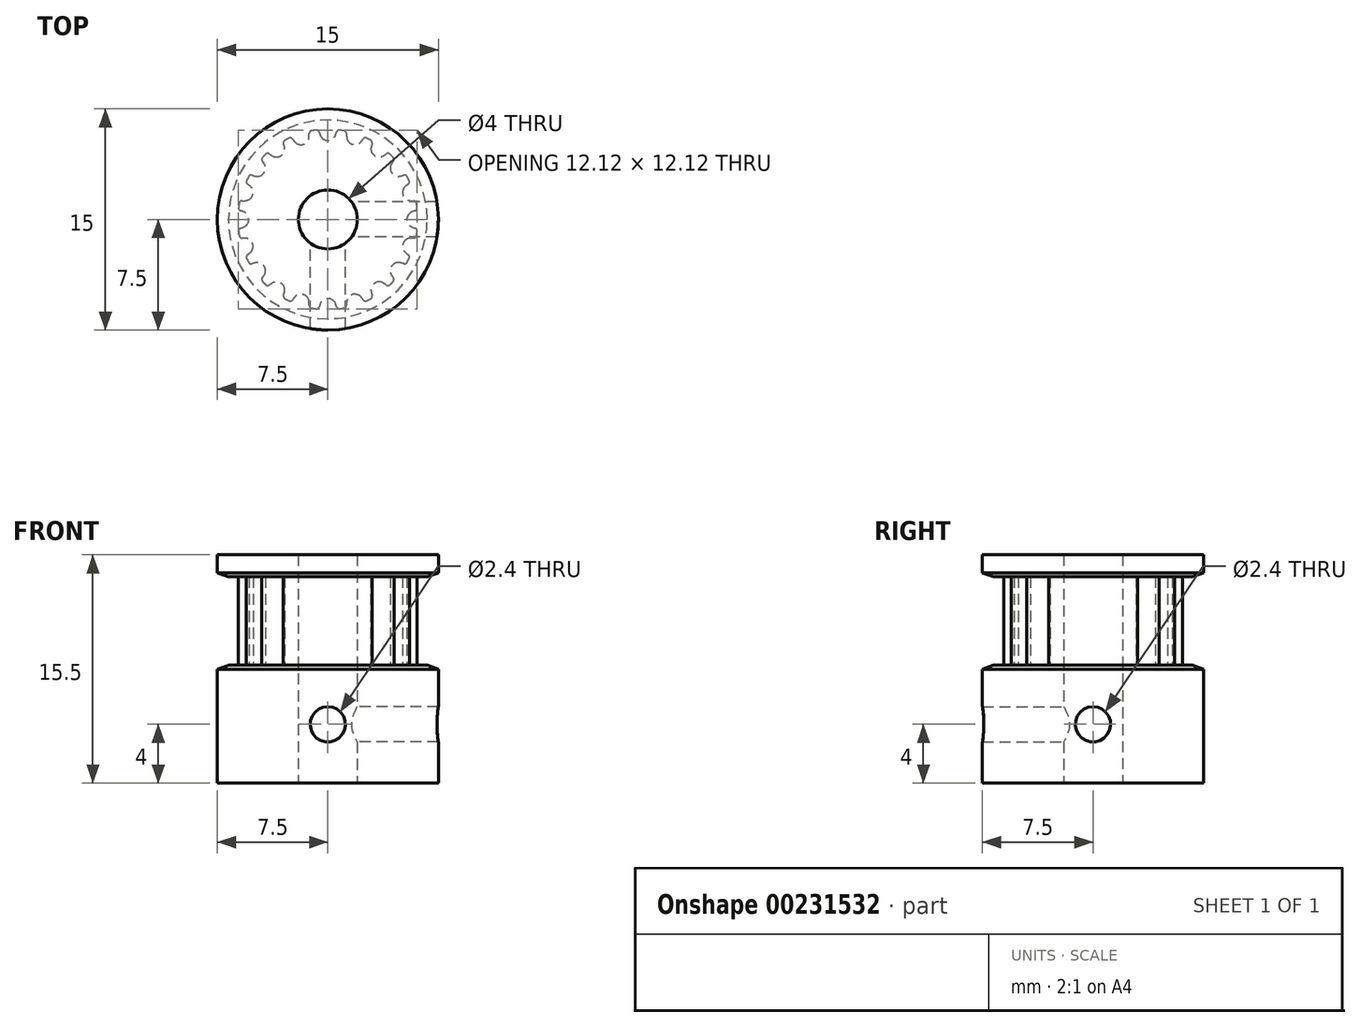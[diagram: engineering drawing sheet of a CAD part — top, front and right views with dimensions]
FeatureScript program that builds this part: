
annotation { "Feature Type Name" : "Feature", "Feature Type Description" : "" }
export const myFeature = defineFeature(function(context is Context, id is Id, definition is map)
    precondition{}
    {
        {
            assignVariable(context, id + "F0", {"name" : "teeth", "anyValue" : 20});
        }
        {
            assignVariable(context, id + "F1", {"name" : "belt_width", "anyValue" : 6 * mm});
        }
        {
            assignVariable(context, id + "F2", {"name" : "bore_diameter", "anyValue" : 4 * mm});
        }
        {
            var Q0;
            Q0=qCreatedBy(makeId("Top.planeOp"),FACE);
            var sketch = newSketch(context, id + "F3", { "sketchPlane" : qUnion([Q0])});
            skLineSegment(sketch, "E0", {"start": v(0, 0) * mm, "end": v(0, 5.36) * mm, "construction": true});
            skCircle(sketch, "E1", {"center": v(0, 0) * mm, "radius": 6.11 * mm});
            skPoint(sketch, "E2.MirrorCS.end.orphan", {"position": v(0.96, 6.04) * mm});
            skLineSegment(sketch, "E3", {"start": v(0.96, 6.04) * mm, "end": v(1, 6.29) * mm, "construction": true});
            skLineSegment(sketch, "E4", {"start": v(-0.96, 6.04) * mm, "end": v(-1, 6.29) * mm, "construction": true});
            skArc(sketch, "E5", {"start": v(0, 5.36) * mm, "mid": v(0.31, 5.46) * mm, "end": v(0.52, 5.72) * mm});
            skArc(sketch, "E6", {"start": v(0.52, 5.72) * mm, "mid": v(0.56, 5.83) * mm, "end": v(0.58, 5.94) * mm, "construction": true});
            skLineSegment(sketch, "E7", {"start": v(0, 5.36) * mm, "end": v(0, 6.11) * mm, "construction": true});
            skLineSegment(sketch, "E8", {"start": v(0, 6.11) * mm, "end": v(0, 6.37) * mm, "construction": true});
            skArc(sketch, "E9", {"start": v(0.58, 5.94) * mm, "mid": v(0.64, 6.04) * mm, "end": v(0.75, 6.07) * mm, "construction": true});
            skArc(sketch, "E10", {"start": v(1, 6.29) * mm, "mid": v(0, 6.37) * mm, "end": v(-1, 6.29) * mm, "construction": true});
            skLineSegment(sketch, "E11", {"start": v(0.96, 6.04) * mm, "end": v(0.84, 5.3) * mm});
            skLineSegment(sketch, "E12", {"start": v(0.84, 5.3) * mm, "end": v(0, 0) * mm});
            skLineSegment(sketch, "E13", {"start": v(0, 0) * mm, "end": v(-0.84, 5.3) * mm});
            skLineSegment(sketch, "E14", {"start": v(-0.84, 5.3) * mm, "end": v(-0.96, 6.04) * mm});
            skArc(sketch, "E15", {"start": v(0.8, 6.06) * mm, "mid": v(0.67, 6.03) * mm, "end": v(0.6, 5.93) * mm});
            skArc(sketch, "E16", {"start": v(0.52, 5.72) * mm, "mid": v(0.56, 5.83) * mm, "end": v(0.6, 5.93) * mm});
            skArc(sketch, "E17.MirrorCS", {"start": v(0, 5.36) * mm, "mid": v(-0.31, 5.46) * mm, "end": v(-0.52, 5.72) * mm});
            skArc(sketch, "E18.MirrorCS", {"start": v(-0.52, 5.72) * mm, "mid": v(-0.56, 5.83) * mm, "end": v(-0.6, 5.93) * mm});
            skArc(sketch, "E19.MirrorCS", {"start": v(-0.8, 6.06) * mm, "mid": v(-0.67, 6.03) * mm, "end": v(-0.6, 5.93) * mm});
            skArc(sketch, "E20", {"start": v(0, 6.11) * mm, "mid": v(-0.2, 6.1) * mm, "end": v(-0.4, 6.1) * mm});
            skArc(sketch, "E21", {"start": v(0.84, 5.3) * mm, "mid": v(0, 5.36) * mm, "end": v(-0.84, 5.3) * mm, "construction": true});
            skLineSegment(sketch, "E22", {"start": v(1, 6.29) * mm, "end": v(1.05, 6.66) * mm, "construction": true});
            skLineSegment(sketch, "E23", {"start": v(-1, 6.29) * mm, "end": v(-1.05, 6.66) * mm, "construction": true});
            skArc(sketch, "E24", {"start": v(-1.05, 6.66) * mm, "mid": v(0, 6.74) * mm, "end": v(1.05, 6.66) * mm, "construction": true});
            skSolve(sketch);
        }
        {
            var Q0;
            Q0=makeQuery(id+"F3.imprint","IMPRINT",FACE,{"disambiguationData":[TD([[makeQuery(id+"F3.imprint","IMPRINT",EDGE,{"derivedFrom":sQuery(id+"F3.wireOp",EDGE,"E5")}),-1.0]])]});
            var Q1;
            {var subQ1=sQuery(id+"F3.wireOp",EDGE,"E14");Q1=makeQuery(id+"F3.imprint","IMPRINT",FACE,{"disambiguationData":[TD([[makeQuery(id+"F3.imprint","IMPRINT",EDGE,{"derivedFrom":subQ1}),-1.0]])]});}
            var Q2;
            {var subQ0=sQuery(id+"F3.wireOp",EDGE,"E12");Q2=makeQuery(id+"F3.imprint","IMPRINT",FACE,{"disambiguationData":[TD([[makeQuery(id+"F3.imprint","IMPRINT",EDGE,{"derivedFrom":subQ0}),-1.0]])]});}
            extrude(context, id + "F4", {"entities" : qUnion([Q0, Q1, Q2]), "endBound" : BoundingType.SYMMETRIC, "depth" : getVariable(context, 'belt_width')});
        }
        {
            var Q0;
            Q0=makeQuery(id+"F4.opExtrude","SWEPT_BODY",BODY,{"disambiguationData":[OSD([sQuery(id+"F3.wireOp",EDGE,"E1"),sQuery(id+"F3.wireOp",EDGE,"E5"),sQuery(id+"F3.wireOp",EDGE,"E11"),sQuery(id+"F3.wireOp",EDGE,"E12"),sQuery(id+"F3.wireOp",EDGE,"E13"),sQuery(id+"F3.wireOp",EDGE,"E14"),sQuery(id+"F3.wireOp",EDGE,"E15"),sQuery(id+"F3.wireOp",EDGE,"E16"),sQuery(id+"F3.wireOp",EDGE,"E17.MirrorCS"),sQuery(id+"F3.wireOp",EDGE,"E18.MirrorCS"),sQuery(id+"F3.wireOp",EDGE,"E19.MirrorCS")])]});
            var Q1;
            Q1=makeQuery(id+"F4.opExtrude","SWEPT_EDGE",EDGE,{"disambiguationData":[OSD([sQuery(id+"F3.wireOp",EDGE,"E12"),sQuery(id+"F3.wireOp",EDGE,"E13")])]});
            circularPattern(context, id + "F5", {"operationType" : NewBodyOperationType.ADD, "entities" : qUnion([Q0]), "axis" : qUnion([Q1]), "angle" : 360 * degree, "instanceCount" : getVariable(context, 'teeth'), "equalSpace" : true});
        }
        {
            var Q0;
            Q0=qCreatedBy(makeId("Front.planeOp"),FACE);
            var sketch = newSketch(context, id + "F6", { "sketchPlane" : qUnion([Q0])});
            skLineSegment(sketch, "E25", {"start": v(0, -3) * mm, "end": v(6.74, -3) * mm});
            skLineSegment(sketch, "E26", {"start": v(6.74, -3) * mm, "end": v(7.5, -3.28) * mm});
            skLineSegment(sketch, "E27", {"start": v(7.5, -3.28) * mm, "end": v(7.5, -11) * mm});
            skLineSegment(sketch, "E28", {"start": v(7.5, -11) * mm, "end": v(0, -11) * mm});
            skLineSegment(sketch, "E29", {"start": v(0, -11) * mm, "end": v(0, -3) * mm});
            skLineSegment(sketch, "E30", {"start": v(0, 3) * mm, "end": v(6.74, 3) * mm});
            skLineSegment(sketch, "E31", {"start": v(7.5, 3.28) * mm, "end": v(6.74, 3) * mm});
            skLineSegment(sketch, "E32", {"start": v(7.5, 3.28) * mm, "end": v(7.5, 4.5) * mm});
            skLineSegment(sketch, "E33", {"start": v(7.5, 4.5) * mm, "end": v(0, 4.5) * mm});
            skLineSegment(sketch, "E34", {"start": v(0, 4.5) * mm, "end": v(0, 3) * mm});
            skLineSegment(sketch, "E35", {"start": v(6.74, -3) * mm, "end": v(7.5, -3) * mm, "construction": true});
            skLineSegment(sketch, "E36", {"start": v(7.5, -3) * mm, "end": v(7.5, -3.28) * mm, "construction": true});
            skLineSegment(sketch, "E37", {"start": v(6.74, 3) * mm, "end": v(7.5, 3) * mm, "construction": true});
            skLineSegment(sketch, "E38", {"start": v(7.5, 3) * mm, "end": v(7.5, 3.28) * mm, "construction": true});
            skLineSegment(sketch, "E39", {"start": v(6.11, 0) * mm, "end": v(6.11, -3) * mm, "construction": true});
            skSolve(sketch);
        }
        {
            var Q0;
            Q0 = qSketchRegion(id + "F6", true);
            var Q1;
            Q1 = qConstructionFilter(qBodyType(qCreatedBy(id + "F6" ,EDGE), BodyType.WIRE), ConstructionObject.NO);
            var Q2;
            Q2=sQuery(id+"F6.wireOp",EDGE,"E29");
            revolve(context, id + "F7", {"operationType" : NewBodyOperationType.ADD, "entities" : qUnion([Q0]), "surfaceEntities" : qUnion([Q1]), "axis" : qUnion([Q2]), "revolveType" : RevolveType.FULL});
        }
        {
            var Q0;
            Q0=makeQuery(id+"F7.opRevolve","SWEPT_FACE",FACE,{"disambiguationData":[OSD([sQuery(id+"F6.wireOp",EDGE,"E28")])]});
            var sketch = newSketch(context, id + "F8", { "sketchPlane" : qUnion([Q0])});
            skPoint(sketch, "E40", {"position": v(0, 0) * mm});
            skSolve(sketch);
        }
        {
            var Q0;
            Q0=sQuery(id+"F8.wireOp",VERTEX,"E40");
            var Q1;
            Q1=makeQuery(id+"F4.opExtrude","SWEPT_BODY",BODY,{"disambiguationData":[OSD([sQuery(id+"F3.wireOp",EDGE,"E1"),sQuery(id+"F3.wireOp",EDGE,"E5"),sQuery(id+"F3.wireOp",EDGE,"E11"),sQuery(id+"F3.wireOp",EDGE,"E12"),sQuery(id+"F3.wireOp",EDGE,"E13"),sQuery(id+"F3.wireOp",EDGE,"E14"),sQuery(id+"F3.wireOp",EDGE,"E15"),sQuery(id+"F3.wireOp",EDGE,"E16"),sQuery(id+"F3.wireOp",EDGE,"E17.MirrorCS"),sQuery(id+"F3.wireOp",EDGE,"E18.MirrorCS"),sQuery(id+"F3.wireOp",EDGE,"E19.MirrorCS")])]});
            hole(context, id + "F9", {"style" : HoleStyle.SIMPLE, "holeDiameter" : getVariable(context, 'bore_diameter'), "endStyle" : HoleEndStyle.THROUGH, "locations" : qUnion([Q0]), "scope" : qUnion([Q1]), "isTappedThrough" : true});
        }
        {
            var Q0;
            Q0=qCreatedBy(makeId("Front.planeOp"),FACE);
            var sketch = newSketch(context, id + "F10", { "sketchPlane" : qUnion([Q0])});
            skPoint(sketch, "E41", {"position": v(0, -7) * mm});
            skLineSegment(sketch, "E42", {"start": v(0, -11) * mm, "end": v(0, -3) * mm});
            skSolve(sketch);
        }
        {
            var Q0;
            Q0=qCreatedBy(makeId("Right.planeOp"),FACE);
            var sketch = newSketch(context, id + "F11", { "sketchPlane" : qUnion([Q0])});
            skPoint(sketch, "E43", {"position": v(0, -7) * mm});
            skSolve(sketch);
        }
        {
            var Q0;
            Q0=sQuery(id+"F10.wireOp",VERTEX,"E41");
            var Q1;
            Q1=makeQuery(id+"F4.opExtrude","SWEPT_BODY",BODY,{"disambiguationData":[OSD([sQuery(id+"F3.wireOp",EDGE,"E1"),sQuery(id+"F3.wireOp",EDGE,"E5"),sQuery(id+"F3.wireOp",EDGE,"E11"),sQuery(id+"F3.wireOp",EDGE,"E12"),sQuery(id+"F3.wireOp",EDGE,"E13"),sQuery(id+"F3.wireOp",EDGE,"E14"),sQuery(id+"F3.wireOp",EDGE,"E15"),sQuery(id+"F3.wireOp",EDGE,"E16"),sQuery(id+"F3.wireOp",EDGE,"E17.MirrorCS"),sQuery(id+"F3.wireOp",EDGE,"E18.MirrorCS"),sQuery(id+"F3.wireOp",EDGE,"E19.MirrorCS")])]});
            hole(context, id + "F12", {"style" : HoleStyle.SIMPLE, "endStyle" : HoleEndStyle.THROUGH, "oppositeDirection" : true, "standardTappedOrClearance" : lookupTablePath({ "standard" : "ISO", "engagement" : "75%", "pitch" : "0.6 mm", "size" : "M3", "type" : "Tapped" }), "standardBlindInLast" : lookupTablePath({ "standard" : "ISO", "engagement" : "75%", "pitch" : "0.6 mm", "size" : "M3", "type" : "Tapped" }), "holeDiameter" : 2.4 * mm, "locations" : qUnion([Q0]), "scope" : qUnion([Q1]), "isTappedThrough" : true, "showTappedDepth" : true});
        }
        {
            var Q0;
            Q0=sQuery(id+"F11.wireOp",VERTEX,"E43");
            var Q1;
            Q1=makeQuery(id+"F4.opExtrude","SWEPT_BODY",BODY,{"disambiguationData":[OSD([sQuery(id+"F3.wireOp",EDGE,"E1"),sQuery(id+"F3.wireOp",EDGE,"E5"),sQuery(id+"F3.wireOp",EDGE,"E11"),sQuery(id+"F3.wireOp",EDGE,"E12"),sQuery(id+"F3.wireOp",EDGE,"E13"),sQuery(id+"F3.wireOp",EDGE,"E14"),sQuery(id+"F3.wireOp",EDGE,"E15"),sQuery(id+"F3.wireOp",EDGE,"E16"),sQuery(id+"F3.wireOp",EDGE,"E17.MirrorCS"),sQuery(id+"F3.wireOp",EDGE,"E18.MirrorCS"),sQuery(id+"F3.wireOp",EDGE,"E19.MirrorCS")])]});
            hole(context, id + "F13", {"style" : HoleStyle.SIMPLE, "endStyle" : HoleEndStyle.THROUGH, "oppositeDirection" : true, "standardTappedOrClearance" : lookupTablePath({ "standard" : "ISO", "engagement" : "75%", "pitch" : "0.6 mm", "size" : "M3", "type" : "Tapped" }), "standardBlindInLast" : lookupTablePath({ "standard" : "ISO", "engagement" : "75%", "pitch" : "0.6 mm", "size" : "M3", "type" : "Tapped" }), "holeDiameter" : 2.4 * mm, "locations" : qUnion([Q0]), "scope" : qUnion([Q1]), "isTappedThrough" : true, "showTappedDepth" : true});
        }
    });
